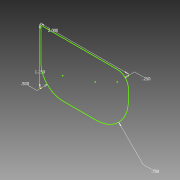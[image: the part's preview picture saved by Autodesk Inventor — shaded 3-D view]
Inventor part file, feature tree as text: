
AUTODESK INVENTOR PART (.ipt)
format: ipt  version: 2015 (Build 190159000, 159)  size: 65,024 bytes
history: native  units: in
note: dims shown in document units (in); Inventor stores cm internally (conversion verified against a paired STEP export)
features: sketch x1
ambient origin geometry x8: Origin, YZ Plane, XZ Plane, XY Plane, X Axis, Y Axis, Z Axis, Center Point
feature tree (1):
  sketch  "Sketch1"  dims[d0=2.0in d1=1.25in d2=0.25in d3=0.75in d4=0.5in]
